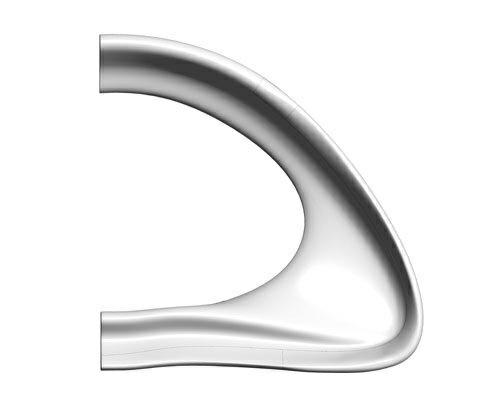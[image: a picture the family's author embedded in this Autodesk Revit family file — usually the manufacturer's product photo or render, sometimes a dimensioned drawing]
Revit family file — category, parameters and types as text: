
# Revit family: CITY ALPHABET litera „V” poziomo_2
name_source: partatom
category: Meble
revit_build: Autodesk Revit 2018 (Build: 20190510_1515(x64)
units: mm (PartAtom-declared; Revit-internal decimal feet)

## family parameters
Numer OmniClass = 23.40.10.11.14
Obiekt nadrzędny = Powierzchnia
Punkt obliczania pomieszczeń = Nie
Tnij formami wycięć po wczytaniu = Nie
Tytuł OmniClass = Exterior Seating
Współdzielony = Nie

## types (1)
- CITY ALPHABET litera „V”
    Domyślna rzędna = 1219 mm
    Długość = 1850 mm  [stored 6.06955 ft]
    IfcExportAs = IfcFurnishingElement
    Komentarze do typu = Ławka
    Materiał - informacja = Szeroki wybór kolorów wg palety RAL. Istnieje również możliwość specjalnego wykonania
kolorystycznego na indywidualne zapytanie klienta.
    Model = CITY ALPHABET litera „V”
    Obraz typu = V.jpg
    Producent = Astrini Design
    Szerokość = 1900 mm  [stored 6.2336 ft]
    Temepratura użytkowania = -40°C do 80°C, ( -40°F do 176°F )
    URL = http://astrini-design.pl
    Waga (szacunkowo) = 80.00 kg
    Waga po wypełnieniu (szacunkowo) = 130.00 kg
    Wysokość = 850 mm  [stored 2.78871 ft]

note: [stored X ft] marks values corroborated as IEEE doubles in the binary element streams (Revit-internal decimal feet)
